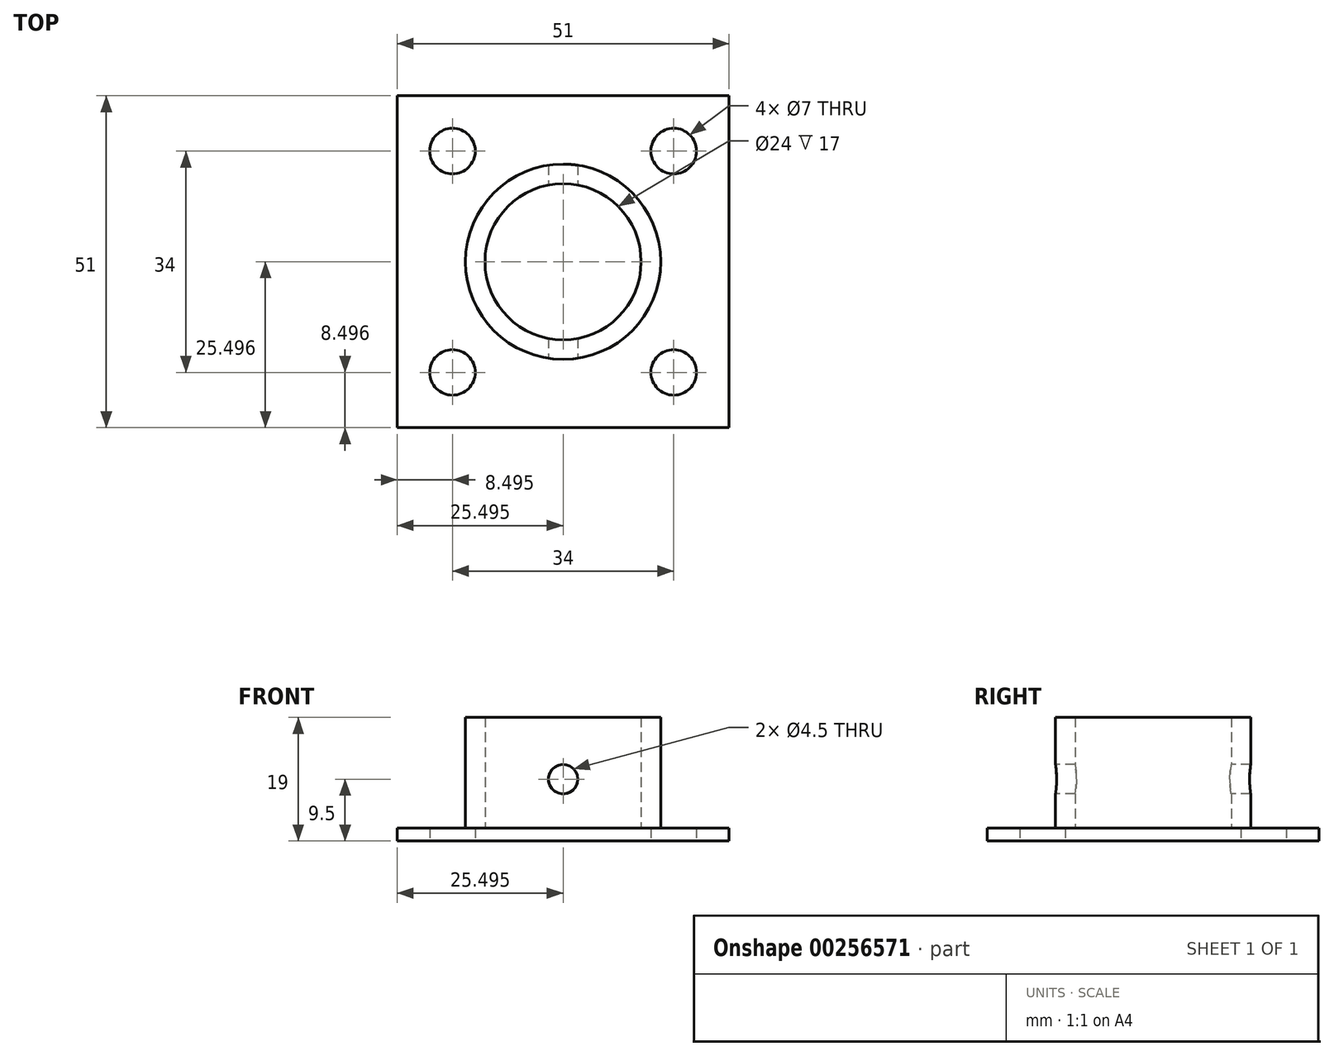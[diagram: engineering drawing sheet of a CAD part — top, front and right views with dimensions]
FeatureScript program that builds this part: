
annotation { "Feature Type Name" : "Feature", "Feature Type Description" : "" }
export const myFeature = defineFeature(function(context is Context, id is Id, definition is map)
    precondition{}
    {
        {
            var Q0;
            Q0=qCreatedBy(makeId("Top.planeOp"),FACE);
            var sketch = newSketch(context, id + "F0", { "sketchPlane" : qUnion([Q0])});
            skLineSegment(sketch, "E0.bottom", {"start": v(-4.78, -4.61) * mm, "end": v(-55.78, -4.61) * mm});
            skLineSegment(sketch, "E0.top", {"start": v(-4.78, 46.39) * mm, "end": v(-55.78, 46.39) * mm});
            skLineSegment(sketch, "E0.left", {"start": v(-4.78, -4.61) * mm, "end": v(-4.78, 46.39) * mm});
            skLineSegment(sketch, "E0.right", {"start": v(-55.78, -4.61) * mm, "end": v(-55.78, 46.39) * mm});
            skPoint(sketch, "E0.middle", {"position": v(-30.28, 20.89) * mm});
            skCircle(sketch, "E1", {"center": v(-47.28, 37.89) * mm, "radius": 3.5 * mm});
            skCircle(sketch, "E2", {"center": v(-13.28, 37.89) * mm, "radius": 3.5 * mm});
            skCircle(sketch, "E3", {"center": v(-47.28, 3.89) * mm, "radius": 3.5 * mm});
            skCircle(sketch, "E4", {"center": v(-13.28, 3.89) * mm, "radius": 3.5 * mm});
            skSolve(sketch);
        }
        {
            var Q0;
            Q0 = qSketchRegion(id + "F0", true);
            extrude(context, id + "F1", {"entities" : qUnion([Q0]), "depth" : 2 * mm});
        }
        {
            var Q0;
            Q0=makeQuery(id+"F1.opExtrude","CAP_FACE",FACE,{"disambiguationData":[OSD([sQuery(id+"F0.wireOp",EDGE,"E0.bottom"),sQuery(id+"F0.wireOp",EDGE,"E0.top"),sQuery(id+"F0.wireOp",EDGE,"E0.left"),sQuery(id+"F0.wireOp",EDGE,"E0.right"),sQuery(id+"F0.wireOp",EDGE,"E1"),sQuery(id+"F0.wireOp",EDGE,"E2"),sQuery(id+"F0.wireOp",EDGE,"E3"),sQuery(id+"F0.wireOp",EDGE,"E4")])],"isStart":false});
            var sketch = newSketch(context, id + "F2", { "sketchPlane" : qUnion([Q0])});
            skCircle(sketch, "E5", {"center": v(-30.28, 20.89) * mm, "radius": 12 * mm});
            skPoint(sketch, "E5.centerSnap0", {"position": v(-4.78, 20.89) * mm});
            skPoint(sketch, "E5.centerSnap1", {"position": v(-30.28, 46.39) * mm});
            skCircle(sketch, "E6", {"center": v(-30.28, 20.89) * mm, "radius": 15 * mm});
            skSolve(sketch);
        }
        {
            var Q0;
            Q0 = qSketchRegion(id + "F2", true);
            extrude(context, id + "F3", {"entities" : qUnion([Q0]), "operationType" : NewBodyOperationType.ADD, "depth" : 17 * mm});
        }
        {
            var Q0;
            {var subQ0=sQuery(id+"F0.wireOp",EDGE,"E0.right");var subQ1=sQuery(id+"F0.wireOp",EDGE,"E0.left");var subQ2=sQuery(id+"F0.wireOp",EDGE,"E0.top");var subQ3=sQuery(id+"F0.wireOp",EDGE,"E0.bottom");var subQ4=sQuery(id+"F0.wireOp",EDGE,"E1");var subQ5=sQuery(id+"F0.wireOp",EDGE,"E2");var subQ6=sQuery(id+"F0.wireOp",EDGE,"E3");var subQ7=sQuery(id+"F0.wireOp",EDGE,"E4");Q0=makeQuery(id+"F3.boolean.opBoolean","SPLIT",FACE,{"disambiguationData":[TD([makeQuery(id+"F1.opExtrude","SWEPT_FACE",FACE,{"disambiguationData":[OSD([subQ3])]})])],"derivedFrom":makeQuery(id+"F1.opExtrude","CAP_FACE",FACE,{"disambiguationData":[OSD([subQ3,subQ2,subQ1,subQ0,subQ4,subQ5,subQ6,subQ7])],"isStart":false})});}
            var sketch = newSketch(context, id + "F4", { "sketchPlane" : qUnion([Q0])});
            skLineSegment(sketch, "E7.bottom", {"start": v(-55.78, -4.61) * mm, "end": v(-4.78, -4.61) * mm});
            skLineSegment(sketch, "E7.top", {"start": v(-55.78, -2.16) * mm, "end": v(-4.78, -2.16) * mm});
            skLineSegment(sketch, "E7.left", {"start": v(-55.78, -4.61) * mm, "end": v(-55.78, -2.16) * mm});
            skLineSegment(sketch, "E7.right", {"start": v(-4.78, -4.61) * mm, "end": v(-4.78, -2.16) * mm});
            skSolve(sketch);
        }
        {
            var Q0;
            Q0 = qSketchRegion(id + "F4", true);
            extrude(context, id + "F5", {"entities" : qUnion([Q0]), "operationType" : NewBodyOperationType.ADD, "depth" : 17 * mm});
        }
        {
            var Q0;
            Q0=makeQuery(id+"F5.boolean.opBoolean","MERGE",FACE,{"derivedFrom":[makeQuery(id+"F1.opExtrude","SWEPT_FACE",FACE,{"disambiguationData":[OSD([sQuery(id+"F0.wireOp",EDGE,"E0.bottom")])]}),makeQuery(id+"F5.opExtrude","SWEPT_FACE",FACE,{"disambiguationData":[OSD([sQuery(id+"F4.wireOp",EDGE,"E7.bottom")])]})]});
            var sketch = newSketch(context, id + "F6", { "sketchPlane" : qUnion([Q0])});
            skCircle(sketch, "E8", {"center": v(-30.28, 9.5) * mm, "radius": 2.25 * mm});
            skPoint(sketch, "E8.centerSnap0", {"position": v(-4.78, 9.5) * mm});
            skPoint(sketch, "E8.centerSnap1", {"position": v(-30.28, 19) * mm});
            skSolve(sketch);
        }
        {
            var Q0;
            Q0 = qSketchRegion(id + "F6", true);
            extrude(context, id + "F7", {"entities" : qUnion([Q0]), "operationType" : NewBodyOperationType.REMOVE, "endBound" : BoundingType.THROUGH_ALL, "oppositeDirection" : true, "depth" : 25 * mm});
        }
        {
            var Q0;
            Q0=makeQuery(id+"F5.opExtrude","CAP_FACE",FACE,{"disambiguationData":[OSD([sQuery(id+"F4.wireOp",EDGE,"E7.bottom"),sQuery(id+"F4.wireOp",EDGE,"E7.top"),sQuery(id+"F4.wireOp",EDGE,"E7.left"),sQuery(id+"F4.wireOp",EDGE,"E7.right")])],"isStart":false});
            var sketch = newSketch(context, id + "F8", { "sketchPlane" : qUnion([Q0])});
            skLineSegment(sketch, "E9.bottom", {"start": v(-55.78, -2.16) * mm, "end": v(-4.78, -2.16) * mm});
            skLineSegment(sketch, "E9.top", {"start": v(-55.78, -4.61) * mm, "end": v(-4.78, -4.61) * mm});
            skLineSegment(sketch, "E9.left", {"start": v(-55.78, -2.16) * mm, "end": v(-55.78, -4.61) * mm});
            skLineSegment(sketch, "E9.right", {"start": v(-4.78, -2.16) * mm, "end": v(-4.78, -4.61) * mm});
            skSolve(sketch);
        }
        {
            var Q0;
            Q0 = qSketchRegion(id + "F8", true);
            extrude(context, id + "F9", {"entities" : qUnion([Q0]), "operationType" : NewBodyOperationType.REMOVE, "oppositeDirection" : true, "depth" : 17 * mm});
        }
    });
